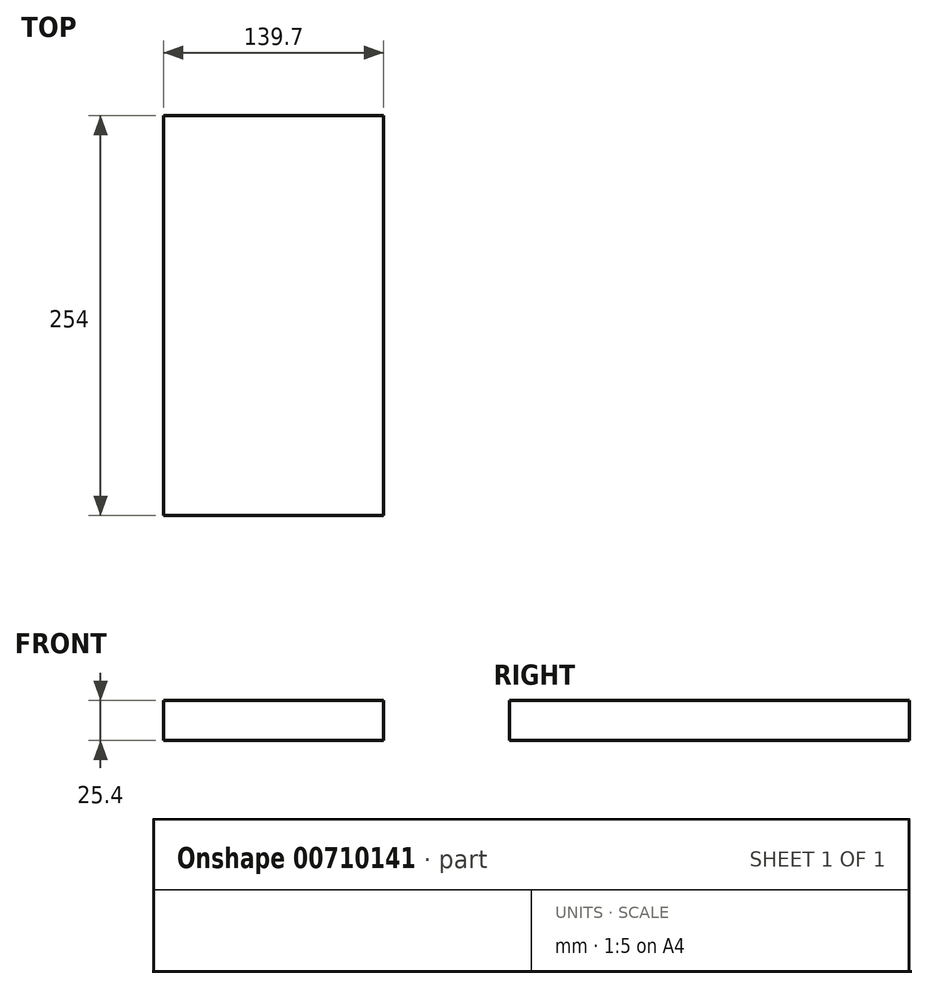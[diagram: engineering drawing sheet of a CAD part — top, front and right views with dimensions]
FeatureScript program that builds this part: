
annotation { "Feature Type Name" : "Feature", "Feature Type Description" : "" }
export const myFeature = defineFeature(function(context is Context, id is Id, definition is map)
    precondition{}
    {
        {
            var Q0;
            Q0=qCreatedBy(makeId("Front.planeOp"),FACE);
            var sketch = newSketch(context, id + "F0", { "sketchPlane" : qUnion([Q0])});
            skLineSegment(sketch, "E0.bottom", {"start": v(-69.85, 12.7) * mm, "end": v(69.85, 12.7) * mm});
            skLineSegment(sketch, "E0.top", {"start": v(-69.85, -12.7) * mm, "end": v(69.85, -12.7) * mm});
            skLineSegment(sketch, "E0.left", {"start": v(-69.85, 12.7) * mm, "end": v(-69.85, -12.7) * mm});
            skLineSegment(sketch, "E0.right", {"start": v(69.85, 12.7) * mm, "end": v(69.85, -12.7) * mm});
            skLineSegment(sketch, "E1", {"start": v(-69.85, 12.7) * mm, "end": v(69.85, -12.7) * mm, "construction": true});
            skSolve(sketch);
        }
        {
            var Q0;
            Q0=makeQuery(id+"F0.imprint","IMPRINT",FACE,{"disambiguationData":[TD([[makeQuery(id+"F0.imprint","IMPRINT",EDGE,{"derivedFrom":sQuery(id+"F0.wireOp",EDGE,"E0.bottom")}),-1.0]])]});
            extrude(context, id + "F1", {"entities" : qUnion([Q0]), "endBound" : BoundingType.SYMMETRIC, "depth" : 254 * mm, "offsetDistance" : 25.4 * mm});
        }
    });
